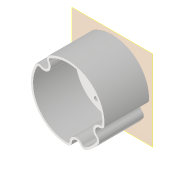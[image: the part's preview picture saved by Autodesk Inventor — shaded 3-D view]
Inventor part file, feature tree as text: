
AUTODESK INVENTOR PART (.ipt)
format: ipt  version: 2022 (Build 260153000, 153)  size: 180,736 bytes
history: native  units: mm
features: extrude x2, sketch x2, other x2, plane x1, reference x1, projected_geometry x1
ambient origin geometry x8: Origin, YZ Plane, XZ Plane, XY Plane, X Axis, Y Axis, Z Axis, Center Point
bodies: Volumenkörper1 (feature_tree)
feature tree (9):
  plane  "Arbeitsebene1"
  extrude  "Extrusion1"  Depth=2.8mm
  extrude  "Extrusion2"  Depth=30.0mm
  sketch  "Skizze1"  dims[d0=2.8mm d1=2.8mm]
  reference  "Referenz1"
  sketch  "Skizze2"  dims[d2=2.8mm d3=2.8mm d4=1.5mm d5=0.0mm d6=1.5mm d7=30.0mm d8=0.0mm]
  projected_geometry  "Projizierte Kontur1"
  other  "Anglerfish_bonne_mamman_m12large_v0.iam"
  other  "Anglerfish_bottom_v0:1"
